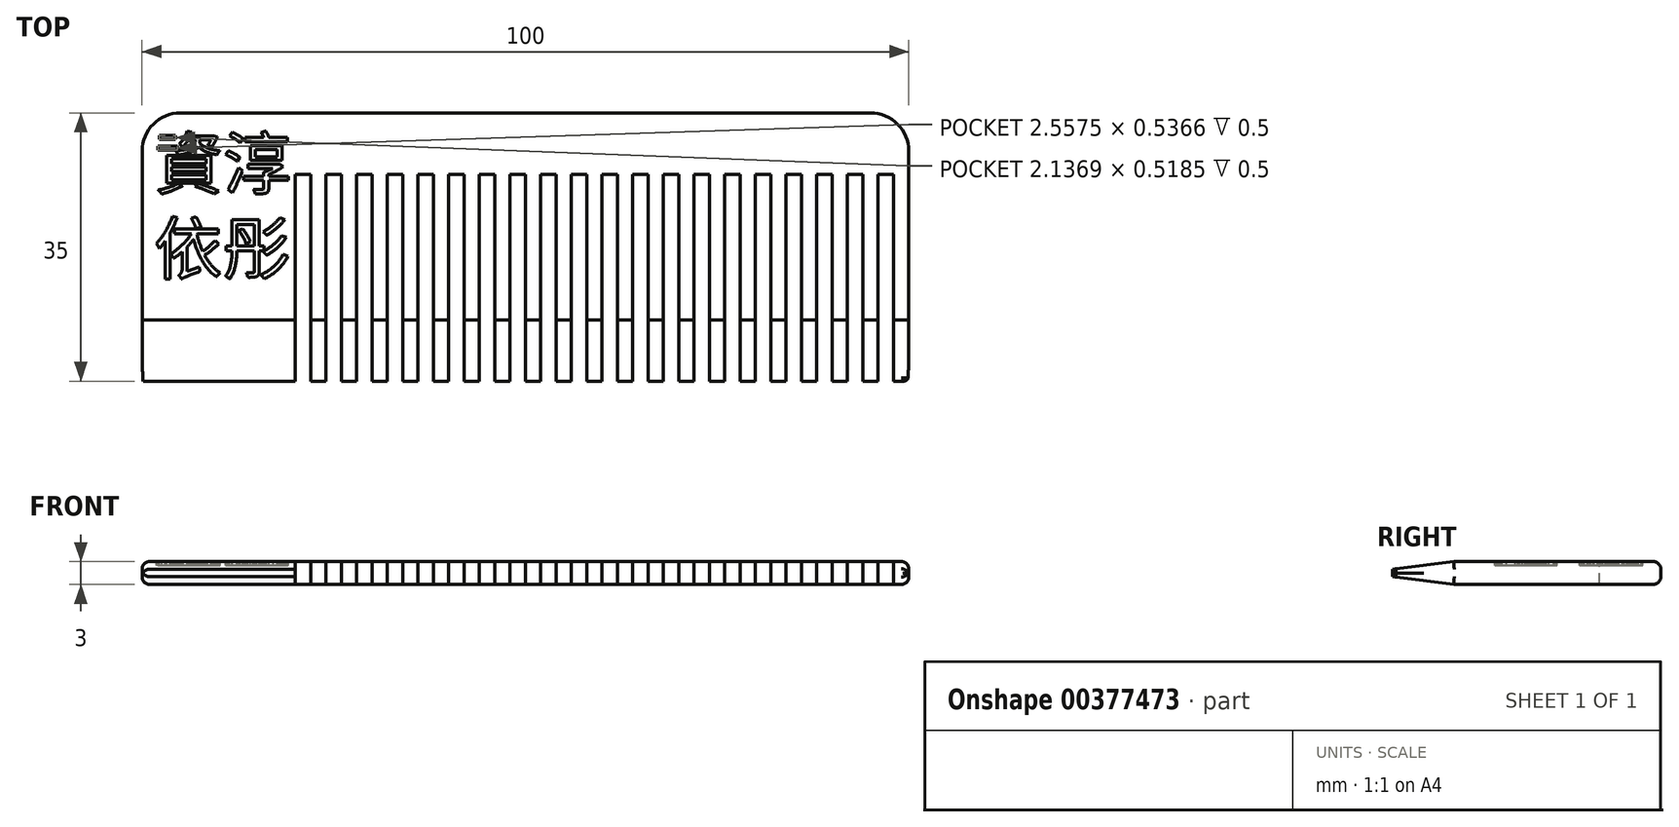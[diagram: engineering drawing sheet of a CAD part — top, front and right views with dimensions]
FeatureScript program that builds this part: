
annotation { "Feature Type Name" : "Feature", "Feature Type Description" : "" }
export const myFeature = defineFeature(function(context is Context, id is Id, definition is map)
    precondition{}
    {
        {
            var Q0;
            Q0=qCreatedBy(makeId("Top.planeOp"),FACE);
            var sketch = newSketch(context, id + "F0", { "sketchPlane" : qUnion([Q0])});
            skLineSegment(sketch, "E0.bottom", {"start": v(-53.48, 49.74) * mm, "end": v(46.52, 49.74) * mm});
            skLineSegment(sketch, "E0.top", {"start": v(-53.48, 14.74) * mm, "end": v(46.52, 14.74) * mm});
            skLineSegment(sketch, "E0.left", {"start": v(-53.48, 49.74) * mm, "end": v(-53.48, 14.74) * mm});
            skLineSegment(sketch, "E0.right", {"start": v(46.52, 49.74) * mm, "end": v(46.52, 14.74) * mm});
            skSolve(sketch);
        }
        {
            var Q0;
            Q0 = qSketchRegion(id + "F0", true);
            extrude(context, id + "F1", {"entities" : qUnion([Q0]), "depth" : 3 * mm});
        }
        {
            var Q0;
            Q0=makeQuery(id+"F1.opExtrude","CAP_FACE",FACE,{"disambiguationData":[OSD([sQuery(id+"F0.wireOp",EDGE,"E0.bottom"),sQuery(id+"F0.wireOp",EDGE,"E0.top"),sQuery(id+"F0.wireOp",EDGE,"E0.left"),sQuery(id+"F0.wireOp",EDGE,"E0.right")])],"isStart":false});
            var sketch = newSketch(context, id + "F2", { "sketchPlane" : qUnion([Q0])});
            skLineSegment(sketch, "E1.bottom", {"start": v(42.52, 41.74) * mm, "end": v(44.52, 41.74) * mm});
            skLineSegment(sketch, "E1.top", {"start": v(42.52, 6.74) * mm, "end": v(44.52, 6.74) * mm});
            skLineSegment(sketch, "E1.left", {"start": v(42.52, 41.74) * mm, "end": v(42.52, 6.74) * mm});
            skLineSegment(sketch, "E1.right", {"start": v(44.52, 41.74) * mm, "end": v(44.52, 6.74) * mm});
            skLineSegment(sketch, "E2.1.0.0", {"start": v(40.52, 41.74) * mm, "end": v(40.52, 6.74) * mm});
            skLineSegment(sketch, "E2.1.0.1", {"start": v(38.52, 41.74) * mm, "end": v(38.52, 6.74) * mm});
            skLineSegment(sketch, "E2.1.0.2", {"start": v(38.52, 6.74) * mm, "end": v(40.52, 6.74) * mm});
            skLineSegment(sketch, "E2.1.0.3", {"start": v(38.52, 41.74) * mm, "end": v(40.52, 41.74) * mm});
            skLineSegment(sketch, "E2.2.0.0", {"start": v(36.52, 41.74) * mm, "end": v(36.52, 6.74) * mm});
            skLineSegment(sketch, "E2.2.0.1", {"start": v(34.52, 41.74) * mm, "end": v(34.52, 6.74) * mm});
            skLineSegment(sketch, "E2.2.0.2", {"start": v(34.52, 6.74) * mm, "end": v(36.52, 6.74) * mm});
            skLineSegment(sketch, "E2.2.0.3", {"start": v(34.52, 41.74) * mm, "end": v(36.52, 41.74) * mm});
            skLineSegment(sketch, "E2.3.0.0", {"start": v(32.52, 41.74) * mm, "end": v(32.52, 6.74) * mm});
            skLineSegment(sketch, "E2.3.0.1", {"start": v(30.52, 41.74) * mm, "end": v(30.52, 6.74) * mm});
            skLineSegment(sketch, "E2.3.0.2", {"start": v(30.52, 6.74) * mm, "end": v(32.52, 6.74) * mm});
            skLineSegment(sketch, "E2.3.0.3", {"start": v(30.52, 41.74) * mm, "end": v(32.52, 41.74) * mm});
            skLineSegment(sketch, "E2.4.0.0", {"start": v(28.52, 41.74) * mm, "end": v(28.52, 6.74) * mm});
            skLineSegment(sketch, "E2.4.0.1", {"start": v(26.52, 41.74) * mm, "end": v(26.52, 6.74) * mm});
            skLineSegment(sketch, "E2.4.0.2", {"start": v(26.52, 6.74) * mm, "end": v(28.52, 6.74) * mm});
            skLineSegment(sketch, "E2.4.0.3", {"start": v(26.52, 41.74) * mm, "end": v(28.52, 41.74) * mm});
            skLineSegment(sketch, "E2.5.0.0", {"start": v(24.52, 41.74) * mm, "end": v(24.52, 6.74) * mm});
            skLineSegment(sketch, "E2.5.0.1", {"start": v(22.52, 41.74) * mm, "end": v(22.52, 6.74) * mm});
            skLineSegment(sketch, "E2.5.0.2", {"start": v(22.52, 6.74) * mm, "end": v(24.52, 6.74) * mm});
            skLineSegment(sketch, "E2.5.0.3", {"start": v(22.52, 41.74) * mm, "end": v(24.52, 41.74) * mm});
            skLineSegment(sketch, "E2.6.0.0", {"start": v(20.52, 41.74) * mm, "end": v(20.52, 6.74) * mm});
            skLineSegment(sketch, "E2.6.0.1", {"start": v(18.52, 41.74) * mm, "end": v(18.52, 6.74) * mm});
            skLineSegment(sketch, "E2.6.0.2", {"start": v(18.52, 6.74) * mm, "end": v(20.52, 6.74) * mm});
            skLineSegment(sketch, "E2.6.0.3", {"start": v(18.52, 41.74) * mm, "end": v(20.52, 41.74) * mm});
            skLineSegment(sketch, "E2.7.0.0", {"start": v(16.52, 41.74) * mm, "end": v(16.52, 6.74) * mm});
            skLineSegment(sketch, "E2.7.0.1", {"start": v(14.52, 41.74) * mm, "end": v(14.52, 6.74) * mm});
            skLineSegment(sketch, "E2.7.0.2", {"start": v(14.52, 6.74) * mm, "end": v(16.52, 6.74) * mm});
            skLineSegment(sketch, "E2.7.0.3", {"start": v(14.52, 41.74) * mm, "end": v(16.52, 41.74) * mm});
            skLineSegment(sketch, "E2.8.0.0", {"start": v(12.52, 41.74) * mm, "end": v(12.52, 6.74) * mm});
            skLineSegment(sketch, "E2.8.0.1", {"start": v(10.52, 41.74) * mm, "end": v(10.52, 6.74) * mm});
            skLineSegment(sketch, "E2.8.0.2", {"start": v(10.52, 6.74) * mm, "end": v(12.52, 6.74) * mm});
            skLineSegment(sketch, "E2.8.0.3", {"start": v(10.52, 41.74) * mm, "end": v(12.52, 41.74) * mm});
            skLineSegment(sketch, "E2.9.0.0", {"start": v(8.52, 41.74) * mm, "end": v(8.52, 6.74) * mm});
            skLineSegment(sketch, "E2.9.0.1", {"start": v(6.52, 41.74) * mm, "end": v(6.52, 6.74) * mm});
            skLineSegment(sketch, "E2.9.0.2", {"start": v(6.52, 6.74) * mm, "end": v(8.52, 6.74) * mm});
            skLineSegment(sketch, "E2.9.0.3", {"start": v(6.52, 41.74) * mm, "end": v(8.52, 41.74) * mm});
            skLineSegment(sketch, "E2.10.0.0", {"start": v(4.52, 41.74) * mm, "end": v(4.52, 6.74) * mm});
            skLineSegment(sketch, "E2.10.0.1", {"start": v(2.52, 41.74) * mm, "end": v(2.52, 6.74) * mm});
            skLineSegment(sketch, "E2.10.0.2", {"start": v(2.52, 6.74) * mm, "end": v(4.52, 6.74) * mm});
            skLineSegment(sketch, "E2.10.0.3", {"start": v(2.52, 41.74) * mm, "end": v(4.52, 41.74) * mm});
            skLineSegment(sketch, "E2.11.0.0", {"start": v(0.52, 41.74) * mm, "end": v(0.52, 6.74) * mm});
            skLineSegment(sketch, "E2.11.0.1", {"start": v(-1.48, 41.74) * mm, "end": v(-1.48, 6.74) * mm});
            skLineSegment(sketch, "E2.11.0.2", {"start": v(-1.48, 6.74) * mm, "end": v(0.52, 6.74) * mm});
            skLineSegment(sketch, "E2.11.0.3", {"start": v(-1.48, 41.74) * mm, "end": v(0.52, 41.74) * mm});
            skLineSegment(sketch, "E2.12.0.0", {"start": v(-3.48, 41.74) * mm, "end": v(-3.48, 6.74) * mm});
            skLineSegment(sketch, "E2.12.0.1", {"start": v(-5.48, 41.74) * mm, "end": v(-5.48, 6.74) * mm});
            skLineSegment(sketch, "E2.12.0.2", {"start": v(-5.48, 6.74) * mm, "end": v(-3.48, 6.74) * mm});
            skLineSegment(sketch, "E2.12.0.3", {"start": v(-5.48, 41.74) * mm, "end": v(-3.48, 41.74) * mm});
            skLineSegment(sketch, "E2.13.0.0", {"start": v(-7.48, 41.74) * mm, "end": v(-7.48, 6.74) * mm});
            skLineSegment(sketch, "E2.13.0.1", {"start": v(-9.48, 41.74) * mm, "end": v(-9.48, 6.74) * mm});
            skLineSegment(sketch, "E2.13.0.2", {"start": v(-9.48, 6.74) * mm, "end": v(-7.48, 6.74) * mm});
            skLineSegment(sketch, "E2.13.0.3", {"start": v(-9.48, 41.74) * mm, "end": v(-7.48, 41.74) * mm});
            skLineSegment(sketch, "E2.14.0.0", {"start": v(-11.48, 41.74) * mm, "end": v(-11.48, 6.74) * mm});
            skLineSegment(sketch, "E2.14.0.1", {"start": v(-13.48, 41.74) * mm, "end": v(-13.48, 6.74) * mm});
            skLineSegment(sketch, "E2.14.0.2", {"start": v(-13.48, 6.74) * mm, "end": v(-11.48, 6.74) * mm});
            skLineSegment(sketch, "E2.14.0.3", {"start": v(-13.48, 41.74) * mm, "end": v(-11.48, 41.74) * mm});
            skLineSegment(sketch, "E2.15.0.0", {"start": v(-15.48, 41.74) * mm, "end": v(-15.48, 6.74) * mm});
            skLineSegment(sketch, "E2.15.0.1", {"start": v(-17.48, 41.74) * mm, "end": v(-17.48, 6.74) * mm});
            skLineSegment(sketch, "E2.15.0.2", {"start": v(-17.48, 6.74) * mm, "end": v(-15.48, 6.74) * mm});
            skLineSegment(sketch, "E2.15.0.3", {"start": v(-17.48, 41.74) * mm, "end": v(-15.48, 41.74) * mm});
            skLineSegment(sketch, "E2.16.0.0", {"start": v(-19.48, 41.74) * mm, "end": v(-19.48, 6.74) * mm});
            skLineSegment(sketch, "E2.16.0.1", {"start": v(-21.48, 41.74) * mm, "end": v(-21.48, 6.74) * mm});
            skLineSegment(sketch, "E2.16.0.2", {"start": v(-21.48, 6.74) * mm, "end": v(-19.48, 6.74) * mm});
            skLineSegment(sketch, "E2.16.0.3", {"start": v(-21.48, 41.74) * mm, "end": v(-19.48, 41.74) * mm});
            skLineSegment(sketch, "E2.17.0.0", {"start": v(-23.48, 41.74) * mm, "end": v(-23.48, 6.74) * mm});
            skLineSegment(sketch, "E2.17.0.1", {"start": v(-25.48, 41.74) * mm, "end": v(-25.48, 6.74) * mm});
            skLineSegment(sketch, "E2.17.0.2", {"start": v(-25.48, 6.74) * mm, "end": v(-23.48, 6.74) * mm});
            skLineSegment(sketch, "E2.17.0.3", {"start": v(-25.48, 41.74) * mm, "end": v(-23.48, 41.74) * mm});
            skLineSegment(sketch, "E2.18.0.0", {"start": v(-27.48, 41.74) * mm, "end": v(-27.48, 6.74) * mm});
            skLineSegment(sketch, "E2.18.0.1", {"start": v(-29.48, 41.74) * mm, "end": v(-29.48, 6.74) * mm});
            skLineSegment(sketch, "E2.18.0.2", {"start": v(-29.48, 6.74) * mm, "end": v(-27.48, 6.74) * mm});
            skLineSegment(sketch, "E2.18.0.3", {"start": v(-29.48, 41.74) * mm, "end": v(-27.48, 41.74) * mm});
            skLineSegment(sketch, "E2.19.0.0", {"start": v(-31.48, 41.74) * mm, "end": v(-31.48, 6.74) * mm});
            skLineSegment(sketch, "E2.19.0.1", {"start": v(-33.48, 41.74) * mm, "end": v(-33.48, 6.74) * mm});
            skLineSegment(sketch, "E2.19.0.2", {"start": v(-33.48, 6.74) * mm, "end": v(-31.48, 6.74) * mm});
            skLineSegment(sketch, "E2.19.0.3", {"start": v(-33.48, 41.74) * mm, "end": v(-31.48, 41.74) * mm});
            skLineSegment(sketch, "E2.direction1", {"start": v(42.52, 6.74) * mm, "end": v(38.52, 6.74) * mm, "construction": true});
            skSolve(sketch);
        }
        {
            var Q0;
            Q0=makeQuery(id+"F1.opExtrude","CAP_EDGE",EDGE,{"disambiguationData":[OSD([sQuery(id+"F0.wireOp",EDGE,"E0.top")])],"isStart":true});
            var Q1;
            Q1=makeQuery(id+"F1.opExtrude","CAP_EDGE",EDGE,{"disambiguationData":[OSD([sQuery(id+"F0.wireOp",EDGE,"E0.top")])],"isStart":false});
            chamfer(context, id + "F3", {"entities" : qUnion([Q0, Q1]), "chamferType" : ChamferType.TWO_OFFSETS, "width1" : 1 * mm, "oppositeDirection" : false, "width2" : 8 * mm, "tangentPropagation" : true});
        }
        {
            var Q0;
            Q0 = qSketchRegion(id + "F2", true);
            extrude(context, id + "F4", {"entities" : qUnion([Q0]), "operationType" : NewBodyOperationType.REMOVE, "oppositeDirection" : true, "depth" : 25 * mm});
        }
        {
            var Q0;
            Q0=makeQuery(id+"F1.opExtrude","CAP_EDGE",EDGE,{"disambiguationData":[OSD([sQuery(id+"F0.wireOp",EDGE,"E0.left")])],"isStart":false});
            var Q1;
            Q1=makeQuery(id+"F1.opExtrude","CAP_EDGE",EDGE,{"disambiguationData":[OSD([sQuery(id+"F0.wireOp",EDGE,"E0.left")])],"isStart":true});
            var Q2;
            Q2=makeQuery(id+"F1.opExtrude","CAP_EDGE",EDGE,{"disambiguationData":[OSD([sQuery(id+"F0.wireOp",EDGE,"E0.bottom")])],"isStart":false});
            var Q3;
            Q3=makeQuery(id+"F1.opExtrude","CAP_EDGE",EDGE,{"disambiguationData":[OSD([sQuery(id+"F0.wireOp",EDGE,"E0.bottom")])],"isStart":true});
            var Q4;
            Q4=makeQuery(id+"F1.opExtrude","CAP_EDGE",EDGE,{"disambiguationData":[OSD([sQuery(id+"F0.wireOp",EDGE,"E0.right")])],"isStart":false});
            var Q5;
            Q5=makeQuery(id+"F1.opExtrude","CAP_EDGE",EDGE,{"disambiguationData":[OSD([sQuery(id+"F0.wireOp",EDGE,"E0.right")])],"isStart":true});
            var Q6;
            Q6=makeQuery(id+"F3.opChamfer","BLEND_EDGE",EDGE,{"blendedFrom":[makeQuery(id+"F1.opExtrude","CAP_EDGE",EDGE,{"disambiguationData":[OSD([sQuery(id+"F0.wireOp",EDGE,"E0.top")])],"isStart":false}),makeQuery(id+"F1.opExtrude","SWEPT_FACE",FACE,{"disambiguationData":[OSD([sQuery(id+"F0.wireOp",EDGE,"E0.left")])]})],"blendedInto":[makeQuery(id+"F1.opExtrude","SWEPT_FACE",FACE,{"disambiguationData":[OSD([sQuery(id+"F0.wireOp",EDGE,"E0.left")])]})]});
            var Q7;
            Q7=makeQuery(id+"F3.opChamfer","BLEND_EDGE",EDGE,{"blendedFrom":[makeQuery(id+"F1.opExtrude","CAP_EDGE",EDGE,{"disambiguationData":[OSD([sQuery(id+"F0.wireOp",EDGE,"E0.top")])],"isStart":true}),makeQuery(id+"F1.opExtrude","SWEPT_FACE",FACE,{"disambiguationData":[OSD([sQuery(id+"F0.wireOp",EDGE,"E0.left")])]})],"blendedInto":[makeQuery(id+"F1.opExtrude","SWEPT_FACE",FACE,{"disambiguationData":[OSD([sQuery(id+"F0.wireOp",EDGE,"E0.left")])]})]});
            var Q8;
            Q8=makeQuery(id+"F3.opChamfer","BLEND_EDGE",EDGE,{"blendedFrom":[makeQuery(id+"F1.opExtrude","CAP_EDGE",EDGE,{"disambiguationData":[OSD([sQuery(id+"F0.wireOp",EDGE,"E0.top")])],"isStart":true}),makeQuery(id+"F1.opExtrude","SWEPT_FACE",FACE,{"disambiguationData":[OSD([sQuery(id+"F0.wireOp",EDGE,"E0.right")])]})],"blendedInto":[makeQuery(id+"F1.opExtrude","SWEPT_FACE",FACE,{"disambiguationData":[OSD([sQuery(id+"F0.wireOp",EDGE,"E0.right")])]})]});
            var Q9;
            Q9=makeQuery(id+"F3.opChamfer","BLEND_EDGE",EDGE,{"blendedFrom":[makeQuery(id+"F1.opExtrude","CAP_EDGE",EDGE,{"disambiguationData":[OSD([sQuery(id+"F0.wireOp",EDGE,"E0.top")])],"isStart":false}),makeQuery(id+"F1.opExtrude","SWEPT_FACE",FACE,{"disambiguationData":[OSD([sQuery(id+"F0.wireOp",EDGE,"E0.right")])]})],"blendedInto":[makeQuery(id+"F1.opExtrude","SWEPT_FACE",FACE,{"disambiguationData":[OSD([sQuery(id+"F0.wireOp",EDGE,"E0.right")])]})]});
            fillet(context, id + "F5", {"entities" : qUnion([Q0, Q1, Q2, Q3, Q4, Q5, Q6, Q7, Q8, Q9]), "radius" : 1 * mm, "tangentPropagation" : true, "allowEdgeOverflow" : false});
        }
        {
            var Q0;
            Q0=makeQuery(id+"F1.opExtrude","SWEPT_EDGE",EDGE,{"disambiguationData":[OSD([sQuery(id+"F0.wireOp",EDGE,"E0.bottom"),sQuery(id+"F0.wireOp",EDGE,"E0.left")])]});
            var Q1;
            Q1=makeQuery(id+"F5.opFillet","BLEND_EDGE",EDGE,{"blendedFrom":[makeQuery(id+"F1.opExtrude","CAP_EDGE",EDGE,{"disambiguationData":[OSD([sQuery(id+"F0.wireOp",EDGE,"E0.bottom")])],"isStart":false}),makeQuery(id+"F1.opExtrude","CAP_EDGE",EDGE,{"disambiguationData":[OSD([sQuery(id+"F0.wireOp",EDGE,"E0.right")])],"isStart":false})],"blendedInto":[]});
            fillet(context, id + "F6", {"entities" : qUnion([Q0, Q1]), "radius" : 5 * mm, "tangentPropagation" : true, "allowEdgeOverflow" : false});
        }
        {
            var Q0;
            {var subQ0=sQuery(id+"F0.wireOp",EDGE,"E0.top");var subQ1=makeQuery(id+"F1.opExtrude","SWEPT_FACE",FACE,{"disambiguationData":[OSD([subQ0])]});var subQ2=makeQuery(id+"F1.opExtrude","CAP_EDGE",EDGE,{"disambiguationData":[OSD([subQ0])],"isStart":false});Q0=makeQuery(id+"F4.boolean.opBoolean","SPLIT",EDGE,{"disambiguationData":[TD([makeQuery(id+"F4.opExtrude","SWEPT_FACE",FACE,{"disambiguationData":[OSD([sQuery(id+"F2.wireOp",EDGE,"E2.18.0.1")])]})])],"derivedFrom":makeQuery(id+"F3.opChamfer","BLEND_EDGE",EDGE,{"blendedFrom":[subQ2,subQ1],"blendedInto":[subQ1]})});}
            var Q1;
            {var subQ0=sQuery(id+"F0.wireOp",EDGE,"E0.top");var subQ1=makeQuery(id+"F1.opExtrude","SWEPT_FACE",FACE,{"disambiguationData":[OSD([subQ0])]});var subQ2=makeQuery(id+"F1.opExtrude","CAP_EDGE",EDGE,{"disambiguationData":[OSD([subQ0])],"isStart":false});Q1=makeQuery(id+"F4.boolean.opBoolean","SPLIT",EDGE,{"disambiguationData":[TD([makeQuery(id+"F4.opExtrude","SWEPT_FACE",FACE,{"disambiguationData":[OSD([sQuery(id+"F2.wireOp",EDGE,"E2.17.0.1")])]})])],"derivedFrom":makeQuery(id+"F3.opChamfer","BLEND_EDGE",EDGE,{"blendedFrom":[subQ2,subQ1],"blendedInto":[subQ1]})});}
            var Q2;
            {var subQ0=sQuery(id+"F0.wireOp",EDGE,"E0.top");var subQ1=makeQuery(id+"F1.opExtrude","SWEPT_FACE",FACE,{"disambiguationData":[OSD([subQ0])]});var subQ2=makeQuery(id+"F1.opExtrude","CAP_EDGE",EDGE,{"disambiguationData":[OSD([subQ0])],"isStart":false});Q2=makeQuery(id+"F4.boolean.opBoolean","SPLIT",EDGE,{"disambiguationData":[TD([makeQuery(id+"F4.opExtrude","SWEPT_FACE",FACE,{"disambiguationData":[OSD([sQuery(id+"F2.wireOp",EDGE,"E2.16.0.1")])]})])],"derivedFrom":makeQuery(id+"F3.opChamfer","BLEND_EDGE",EDGE,{"blendedFrom":[subQ2,subQ1],"blendedInto":[subQ1]})});}
            var Q3;
            {var subQ0=sQuery(id+"F0.wireOp",EDGE,"E0.top");var subQ1=makeQuery(id+"F1.opExtrude","SWEPT_FACE",FACE,{"disambiguationData":[OSD([subQ0])]});var subQ2=makeQuery(id+"F1.opExtrude","CAP_EDGE",EDGE,{"disambiguationData":[OSD([subQ0])],"isStart":false});Q3=makeQuery(id+"F4.boolean.opBoolean","SPLIT",EDGE,{"disambiguationData":[TD([makeQuery(id+"F4.opExtrude","SWEPT_FACE",FACE,{"disambiguationData":[OSD([sQuery(id+"F2.wireOp",EDGE,"E2.15.0.1")])]})])],"derivedFrom":makeQuery(id+"F3.opChamfer","BLEND_EDGE",EDGE,{"blendedFrom":[subQ2,subQ1],"blendedInto":[subQ1]})});}
            var Q4;
            {var subQ0=sQuery(id+"F0.wireOp",EDGE,"E0.top");var subQ1=makeQuery(id+"F1.opExtrude","SWEPT_FACE",FACE,{"disambiguationData":[OSD([subQ0])]});var subQ2=makeQuery(id+"F1.opExtrude","CAP_EDGE",EDGE,{"disambiguationData":[OSD([subQ0])],"isStart":false});Q4=makeQuery(id+"F4.boolean.opBoolean","SPLIT",EDGE,{"disambiguationData":[TD([makeQuery(id+"F4.opExtrude","SWEPT_FACE",FACE,{"disambiguationData":[OSD([sQuery(id+"F2.wireOp",EDGE,"E2.14.0.1")])]})])],"derivedFrom":makeQuery(id+"F3.opChamfer","BLEND_EDGE",EDGE,{"blendedFrom":[subQ2,subQ1],"blendedInto":[subQ1]})});}
            var Q5;
            {var subQ0=sQuery(id+"F0.wireOp",EDGE,"E0.top");var subQ1=makeQuery(id+"F1.opExtrude","SWEPT_FACE",FACE,{"disambiguationData":[OSD([subQ0])]});var subQ2=makeQuery(id+"F1.opExtrude","CAP_EDGE",EDGE,{"disambiguationData":[OSD([subQ0])],"isStart":false});Q5=makeQuery(id+"F4.boolean.opBoolean","SPLIT",EDGE,{"disambiguationData":[TD([makeQuery(id+"F4.opExtrude","SWEPT_FACE",FACE,{"disambiguationData":[OSD([sQuery(id+"F2.wireOp",EDGE,"E2.13.0.1")])]})])],"derivedFrom":makeQuery(id+"F3.opChamfer","BLEND_EDGE",EDGE,{"blendedFrom":[subQ2,subQ1],"blendedInto":[subQ1]})});}
            var Q6;
            {var subQ0=sQuery(id+"F0.wireOp",EDGE,"E0.top");var subQ1=makeQuery(id+"F1.opExtrude","SWEPT_FACE",FACE,{"disambiguationData":[OSD([subQ0])]});var subQ2=makeQuery(id+"F1.opExtrude","CAP_EDGE",EDGE,{"disambiguationData":[OSD([subQ0])],"isStart":false});Q6=makeQuery(id+"F4.boolean.opBoolean","SPLIT",EDGE,{"disambiguationData":[TD([makeQuery(id+"F4.opExtrude","SWEPT_FACE",FACE,{"disambiguationData":[OSD([sQuery(id+"F2.wireOp",EDGE,"E2.12.0.1")])]})])],"derivedFrom":makeQuery(id+"F3.opChamfer","BLEND_EDGE",EDGE,{"blendedFrom":[subQ2,subQ1],"blendedInto":[subQ1]})});}
            var Q7;
            {var subQ0=sQuery(id+"F0.wireOp",EDGE,"E0.top");var subQ1=makeQuery(id+"F1.opExtrude","SWEPT_FACE",FACE,{"disambiguationData":[OSD([subQ0])]});var subQ2=makeQuery(id+"F1.opExtrude","CAP_EDGE",EDGE,{"disambiguationData":[OSD([subQ0])],"isStart":false});Q7=makeQuery(id+"F4.boolean.opBoolean","SPLIT",EDGE,{"disambiguationData":[TD([makeQuery(id+"F4.opExtrude","SWEPT_FACE",FACE,{"disambiguationData":[OSD([sQuery(id+"F2.wireOp",EDGE,"E2.11.0.1")])]})])],"derivedFrom":makeQuery(id+"F3.opChamfer","BLEND_EDGE",EDGE,{"blendedFrom":[subQ2,subQ1],"blendedInto":[subQ1]})});}
            var Q8;
            {var subQ0=sQuery(id+"F0.wireOp",EDGE,"E0.top");var subQ1=makeQuery(id+"F1.opExtrude","SWEPT_FACE",FACE,{"disambiguationData":[OSD([subQ0])]});var subQ2=makeQuery(id+"F1.opExtrude","CAP_EDGE",EDGE,{"disambiguationData":[OSD([subQ0])],"isStart":false});Q8=makeQuery(id+"F4.boolean.opBoolean","SPLIT",EDGE,{"disambiguationData":[TD([makeQuery(id+"F4.opExtrude","SWEPT_FACE",FACE,{"disambiguationData":[OSD([sQuery(id+"F2.wireOp",EDGE,"E2.10.0.1")])]})])],"derivedFrom":makeQuery(id+"F3.opChamfer","BLEND_EDGE",EDGE,{"blendedFrom":[subQ2,subQ1],"blendedInto":[subQ1]})});}
            var Q9;
            {var subQ0=sQuery(id+"F0.wireOp",EDGE,"E0.top");var subQ1=makeQuery(id+"F1.opExtrude","SWEPT_FACE",FACE,{"disambiguationData":[OSD([subQ0])]});var subQ2=makeQuery(id+"F1.opExtrude","CAP_EDGE",EDGE,{"disambiguationData":[OSD([subQ0])],"isStart":false});Q9=makeQuery(id+"F4.boolean.opBoolean","SPLIT",EDGE,{"disambiguationData":[TD([makeQuery(id+"F4.opExtrude","SWEPT_FACE",FACE,{"disambiguationData":[OSD([sQuery(id+"F2.wireOp",EDGE,"E2.9.0.1")])]})])],"derivedFrom":makeQuery(id+"F3.opChamfer","BLEND_EDGE",EDGE,{"blendedFrom":[subQ2,subQ1],"blendedInto":[subQ1]})});}
            var Q10;
            {var subQ0=sQuery(id+"F0.wireOp",EDGE,"E0.top");var subQ1=makeQuery(id+"F1.opExtrude","SWEPT_FACE",FACE,{"disambiguationData":[OSD([subQ0])]});var subQ2=makeQuery(id+"F1.opExtrude","CAP_EDGE",EDGE,{"disambiguationData":[OSD([subQ0])],"isStart":false});Q10=makeQuery(id+"F4.boolean.opBoolean","SPLIT",EDGE,{"disambiguationData":[TD([makeQuery(id+"F4.opExtrude","SWEPT_FACE",FACE,{"disambiguationData":[OSD([sQuery(id+"F2.wireOp",EDGE,"E2.8.0.1")])]})])],"derivedFrom":makeQuery(id+"F3.opChamfer","BLEND_EDGE",EDGE,{"blendedFrom":[subQ2,subQ1],"blendedInto":[subQ1]})});}
            var Q11;
            {var subQ0=sQuery(id+"F0.wireOp",EDGE,"E0.top");var subQ1=makeQuery(id+"F1.opExtrude","SWEPT_FACE",FACE,{"disambiguationData":[OSD([subQ0])]});var subQ2=makeQuery(id+"F1.opExtrude","CAP_EDGE",EDGE,{"disambiguationData":[OSD([subQ0])],"isStart":false});Q11=makeQuery(id+"F4.boolean.opBoolean","SPLIT",EDGE,{"disambiguationData":[TD([makeQuery(id+"F4.opExtrude","SWEPT_FACE",FACE,{"disambiguationData":[OSD([sQuery(id+"F2.wireOp",EDGE,"E2.7.0.1")])]})])],"derivedFrom":makeQuery(id+"F3.opChamfer","BLEND_EDGE",EDGE,{"blendedFrom":[subQ2,subQ1],"blendedInto":[subQ1]})});}
            var Q12;
            {var subQ0=sQuery(id+"F0.wireOp",EDGE,"E0.top");var subQ1=makeQuery(id+"F1.opExtrude","SWEPT_FACE",FACE,{"disambiguationData":[OSD([subQ0])]});var subQ2=makeQuery(id+"F1.opExtrude","CAP_EDGE",EDGE,{"disambiguationData":[OSD([subQ0])],"isStart":false});Q12=makeQuery(id+"F4.boolean.opBoolean","SPLIT",EDGE,{"disambiguationData":[TD([makeQuery(id+"F4.opExtrude","SWEPT_FACE",FACE,{"disambiguationData":[OSD([sQuery(id+"F2.wireOp",EDGE,"E2.5.0.1")])]})])],"derivedFrom":makeQuery(id+"F3.opChamfer","BLEND_EDGE",EDGE,{"blendedFrom":[subQ2,subQ1],"blendedInto":[subQ1]})});}
            var Q13;
            {var subQ0=sQuery(id+"F0.wireOp",EDGE,"E0.top");var subQ1=makeQuery(id+"F1.opExtrude","SWEPT_FACE",FACE,{"disambiguationData":[OSD([subQ0])]});var subQ2=makeQuery(id+"F1.opExtrude","CAP_EDGE",EDGE,{"disambiguationData":[OSD([subQ0])],"isStart":false});Q13=makeQuery(id+"F4.boolean.opBoolean","SPLIT",EDGE,{"disambiguationData":[TD([makeQuery(id+"F4.opExtrude","SWEPT_FACE",FACE,{"disambiguationData":[OSD([sQuery(id+"F2.wireOp",EDGE,"E2.4.0.1")])]})])],"derivedFrom":makeQuery(id+"F3.opChamfer","BLEND_EDGE",EDGE,{"blendedFrom":[subQ2,subQ1],"blendedInto":[subQ1]})});}
            var Q14;
            {var subQ0=sQuery(id+"F0.wireOp",EDGE,"E0.top");var subQ1=makeQuery(id+"F1.opExtrude","SWEPT_FACE",FACE,{"disambiguationData":[OSD([subQ0])]});var subQ2=makeQuery(id+"F1.opExtrude","CAP_EDGE",EDGE,{"disambiguationData":[OSD([subQ0])],"isStart":false});Q14=makeQuery(id+"F4.boolean.opBoolean","SPLIT",EDGE,{"disambiguationData":[TD([makeQuery(id+"F4.opExtrude","SWEPT_FACE",FACE,{"disambiguationData":[OSD([sQuery(id+"F2.wireOp",EDGE,"E2.3.0.1")])]})])],"derivedFrom":makeQuery(id+"F3.opChamfer","BLEND_EDGE",EDGE,{"blendedFrom":[subQ2,subQ1],"blendedInto":[subQ1]})});}
            var Q15;
            {var subQ0=sQuery(id+"F0.wireOp",EDGE,"E0.top");var subQ1=makeQuery(id+"F1.opExtrude","SWEPT_FACE",FACE,{"disambiguationData":[OSD([subQ0])]});var subQ2=makeQuery(id+"F1.opExtrude","CAP_EDGE",EDGE,{"disambiguationData":[OSD([subQ0])],"isStart":false});Q15=makeQuery(id+"F4.boolean.opBoolean","SPLIT",EDGE,{"disambiguationData":[TD([makeQuery(id+"F4.opExtrude","SWEPT_FACE",FACE,{"disambiguationData":[OSD([sQuery(id+"F2.wireOp",EDGE,"E2.2.0.1")])]})])],"derivedFrom":makeQuery(id+"F3.opChamfer","BLEND_EDGE",EDGE,{"blendedFrom":[subQ2,subQ1],"blendedInto":[subQ1]})});}
            var Q16;
            {var subQ0=sQuery(id+"F0.wireOp",EDGE,"E0.top");var subQ1=makeQuery(id+"F1.opExtrude","SWEPT_FACE",FACE,{"disambiguationData":[OSD([subQ0])]});var subQ2=makeQuery(id+"F1.opExtrude","CAP_EDGE",EDGE,{"disambiguationData":[OSD([subQ0])],"isStart":false});Q16=makeQuery(id+"F4.boolean.opBoolean","SPLIT",EDGE,{"disambiguationData":[TD([makeQuery(id+"F4.opExtrude","SWEPT_FACE",FACE,{"disambiguationData":[OSD([sQuery(id+"F2.wireOp",EDGE,"E2.1.0.1")])]})])],"derivedFrom":makeQuery(id+"F3.opChamfer","BLEND_EDGE",EDGE,{"blendedFrom":[subQ2,subQ1],"blendedInto":[subQ1]})});}
            var Q17;
            {var subQ0=sQuery(id+"F0.wireOp",EDGE,"E0.top");var subQ1=makeQuery(id+"F1.opExtrude","SWEPT_FACE",FACE,{"disambiguationData":[OSD([subQ0])]});var subQ2=makeQuery(id+"F1.opExtrude","CAP_EDGE",EDGE,{"disambiguationData":[OSD([subQ0])],"isStart":false});Q17=makeQuery(id+"F4.boolean.opBoolean","SPLIT",EDGE,{"disambiguationData":[TD([makeQuery(id+"F4.opExtrude","SWEPT_FACE",FACE,{"disambiguationData":[OSD([sQuery(id+"F2.wireOp",EDGE,"E1.left")])]})])],"derivedFrom":makeQuery(id+"F3.opChamfer","BLEND_EDGE",EDGE,{"blendedFrom":[subQ2,subQ1],"blendedInto":[subQ1]})});}
            var Q18;
            {var subQ0=sQuery(id+"F0.wireOp",EDGE,"E0.top");var subQ1=makeQuery(id+"F1.opExtrude","SWEPT_FACE",FACE,{"disambiguationData":[OSD([subQ0])]});var subQ2=makeQuery(id+"F1.opExtrude","CAP_EDGE",EDGE,{"disambiguationData":[OSD([subQ0])],"isStart":false});Q18=makeQuery(id+"F4.boolean.opBoolean","SPLIT",EDGE,{"disambiguationData":[TD([makeQuery(id+"F4.opExtrude","SWEPT_FACE",FACE,{"disambiguationData":[OSD([sQuery(id+"F2.wireOp",EDGE,"E2.6.0.1")])]})])],"derivedFrom":makeQuery(id+"F3.opChamfer","BLEND_EDGE",EDGE,{"blendedFrom":[subQ2,subQ1],"blendedInto":[subQ1]})});}
            var Q19;
            {var subQ0=sQuery(id+"F0.wireOp",EDGE,"E0.top");var subQ1=makeQuery(id+"F1.opExtrude","SWEPT_FACE",FACE,{"disambiguationData":[OSD([subQ0])]});var subQ2=makeQuery(id+"F1.opExtrude","CAP_EDGE",EDGE,{"disambiguationData":[OSD([subQ0])],"isStart":true});Q19=makeQuery(id+"F4.boolean.opBoolean","SPLIT",EDGE,{"disambiguationData":[TD([makeQuery(id+"F4.opExtrude","SWEPT_FACE",FACE,{"disambiguationData":[OSD([sQuery(id+"F2.wireOp",EDGE,"E2.18.0.1")])]})])],"derivedFrom":makeQuery(id+"F3.opChamfer","BLEND_EDGE",EDGE,{"blendedFrom":[subQ2,subQ1],"blendedInto":[subQ1]})});}
            var Q20;
            {var subQ0=sQuery(id+"F0.wireOp",EDGE,"E0.top");var subQ1=makeQuery(id+"F1.opExtrude","SWEPT_FACE",FACE,{"disambiguationData":[OSD([subQ0])]});var subQ2=makeQuery(id+"F1.opExtrude","CAP_EDGE",EDGE,{"disambiguationData":[OSD([subQ0])],"isStart":true});Q20=makeQuery(id+"F4.boolean.opBoolean","SPLIT",EDGE,{"disambiguationData":[TD([makeQuery(id+"F4.opExtrude","SWEPT_FACE",FACE,{"disambiguationData":[OSD([sQuery(id+"F2.wireOp",EDGE,"E2.17.0.1")])]})])],"derivedFrom":makeQuery(id+"F3.opChamfer","BLEND_EDGE",EDGE,{"blendedFrom":[subQ2,subQ1],"blendedInto":[subQ1]})});}
            var Q21;
            {var subQ0=sQuery(id+"F0.wireOp",EDGE,"E0.top");var subQ1=makeQuery(id+"F1.opExtrude","SWEPT_FACE",FACE,{"disambiguationData":[OSD([subQ0])]});var subQ2=makeQuery(id+"F1.opExtrude","CAP_EDGE",EDGE,{"disambiguationData":[OSD([subQ0])],"isStart":true});Q21=makeQuery(id+"F4.boolean.opBoolean","SPLIT",EDGE,{"disambiguationData":[TD([makeQuery(id+"F4.opExtrude","SWEPT_FACE",FACE,{"disambiguationData":[OSD([sQuery(id+"F2.wireOp",EDGE,"E2.16.0.1")])]})])],"derivedFrom":makeQuery(id+"F3.opChamfer","BLEND_EDGE",EDGE,{"blendedFrom":[subQ2,subQ1],"blendedInto":[subQ1]})});}
            var Q22;
            {var subQ0=sQuery(id+"F0.wireOp",EDGE,"E0.top");var subQ1=makeQuery(id+"F1.opExtrude","SWEPT_FACE",FACE,{"disambiguationData":[OSD([subQ0])]});var subQ2=makeQuery(id+"F1.opExtrude","CAP_EDGE",EDGE,{"disambiguationData":[OSD([subQ0])],"isStart":true});Q22=makeQuery(id+"F4.boolean.opBoolean","SPLIT",EDGE,{"disambiguationData":[TD([makeQuery(id+"F4.opExtrude","SWEPT_FACE",FACE,{"disambiguationData":[OSD([sQuery(id+"F2.wireOp",EDGE,"E2.15.0.1")])]})])],"derivedFrom":makeQuery(id+"F3.opChamfer","BLEND_EDGE",EDGE,{"blendedFrom":[subQ2,subQ1],"blendedInto":[subQ1]})});}
            var Q23;
            {var subQ0=sQuery(id+"F0.wireOp",EDGE,"E0.top");var subQ1=makeQuery(id+"F1.opExtrude","SWEPT_FACE",FACE,{"disambiguationData":[OSD([subQ0])]});var subQ2=makeQuery(id+"F1.opExtrude","CAP_EDGE",EDGE,{"disambiguationData":[OSD([subQ0])],"isStart":true});Q23=makeQuery(id+"F4.boolean.opBoolean","SPLIT",EDGE,{"disambiguationData":[TD([makeQuery(id+"F4.opExtrude","SWEPT_FACE",FACE,{"disambiguationData":[OSD([sQuery(id+"F2.wireOp",EDGE,"E2.14.0.1")])]})])],"derivedFrom":makeQuery(id+"F3.opChamfer","BLEND_EDGE",EDGE,{"blendedFrom":[subQ2,subQ1],"blendedInto":[subQ1]})});}
            var Q24;
            {var subQ0=sQuery(id+"F0.wireOp",EDGE,"E0.top");var subQ1=makeQuery(id+"F1.opExtrude","SWEPT_FACE",FACE,{"disambiguationData":[OSD([subQ0])]});var subQ2=makeQuery(id+"F1.opExtrude","CAP_EDGE",EDGE,{"disambiguationData":[OSD([subQ0])],"isStart":true});Q24=makeQuery(id+"F4.boolean.opBoolean","SPLIT",EDGE,{"disambiguationData":[TD([makeQuery(id+"F4.opExtrude","SWEPT_FACE",FACE,{"disambiguationData":[OSD([sQuery(id+"F2.wireOp",EDGE,"E2.13.0.1")])]})])],"derivedFrom":makeQuery(id+"F3.opChamfer","BLEND_EDGE",EDGE,{"blendedFrom":[subQ2,subQ1],"blendedInto":[subQ1]})});}
            var Q25;
            {var subQ0=sQuery(id+"F0.wireOp",EDGE,"E0.top");var subQ1=makeQuery(id+"F1.opExtrude","SWEPT_FACE",FACE,{"disambiguationData":[OSD([subQ0])]});var subQ2=makeQuery(id+"F1.opExtrude","CAP_EDGE",EDGE,{"disambiguationData":[OSD([subQ0])],"isStart":true});Q25=makeQuery(id+"F4.boolean.opBoolean","SPLIT",EDGE,{"disambiguationData":[TD([makeQuery(id+"F4.opExtrude","SWEPT_FACE",FACE,{"disambiguationData":[OSD([sQuery(id+"F2.wireOp",EDGE,"E2.12.0.1")])]})])],"derivedFrom":makeQuery(id+"F3.opChamfer","BLEND_EDGE",EDGE,{"blendedFrom":[subQ2,subQ1],"blendedInto":[subQ1]})});}
            var Q26;
            {var subQ0=sQuery(id+"F0.wireOp",EDGE,"E0.top");var subQ1=makeQuery(id+"F1.opExtrude","SWEPT_FACE",FACE,{"disambiguationData":[OSD([subQ0])]});var subQ2=makeQuery(id+"F1.opExtrude","CAP_EDGE",EDGE,{"disambiguationData":[OSD([subQ0])],"isStart":true});Q26=makeQuery(id+"F4.boolean.opBoolean","SPLIT",EDGE,{"disambiguationData":[TD([makeQuery(id+"F4.opExtrude","SWEPT_FACE",FACE,{"disambiguationData":[OSD([sQuery(id+"F2.wireOp",EDGE,"E2.11.0.1")])]})])],"derivedFrom":makeQuery(id+"F3.opChamfer","BLEND_EDGE",EDGE,{"blendedFrom":[subQ2,subQ1],"blendedInto":[subQ1]})});}
            var Q27;
            {var subQ0=sQuery(id+"F0.wireOp",EDGE,"E0.top");var subQ1=makeQuery(id+"F1.opExtrude","SWEPT_FACE",FACE,{"disambiguationData":[OSD([subQ0])]});var subQ2=makeQuery(id+"F1.opExtrude","CAP_EDGE",EDGE,{"disambiguationData":[OSD([subQ0])],"isStart":true});Q27=makeQuery(id+"F4.boolean.opBoolean","SPLIT",EDGE,{"disambiguationData":[TD([makeQuery(id+"F4.opExtrude","SWEPT_FACE",FACE,{"disambiguationData":[OSD([sQuery(id+"F2.wireOp",EDGE,"E2.10.0.1")])]})])],"derivedFrom":makeQuery(id+"F3.opChamfer","BLEND_EDGE",EDGE,{"blendedFrom":[subQ2,subQ1],"blendedInto":[subQ1]})});}
            var Q28;
            {var subQ0=sQuery(id+"F0.wireOp",EDGE,"E0.top");var subQ1=makeQuery(id+"F1.opExtrude","SWEPT_FACE",FACE,{"disambiguationData":[OSD([subQ0])]});var subQ2=makeQuery(id+"F1.opExtrude","CAP_EDGE",EDGE,{"disambiguationData":[OSD([subQ0])],"isStart":true});Q28=makeQuery(id+"F4.boolean.opBoolean","SPLIT",EDGE,{"disambiguationData":[TD([makeQuery(id+"F4.opExtrude","SWEPT_FACE",FACE,{"disambiguationData":[OSD([sQuery(id+"F2.wireOp",EDGE,"E2.9.0.1")])]})])],"derivedFrom":makeQuery(id+"F3.opChamfer","BLEND_EDGE",EDGE,{"blendedFrom":[subQ2,subQ1],"blendedInto":[subQ1]})});}
            var Q29;
            {var subQ0=sQuery(id+"F0.wireOp",EDGE,"E0.top");var subQ1=makeQuery(id+"F1.opExtrude","SWEPT_FACE",FACE,{"disambiguationData":[OSD([subQ0])]});var subQ2=makeQuery(id+"F1.opExtrude","CAP_EDGE",EDGE,{"disambiguationData":[OSD([subQ0])],"isStart":true});Q29=makeQuery(id+"F4.boolean.opBoolean","SPLIT",EDGE,{"disambiguationData":[TD([makeQuery(id+"F4.opExtrude","SWEPT_FACE",FACE,{"disambiguationData":[OSD([sQuery(id+"F2.wireOp",EDGE,"E2.8.0.1")])]})])],"derivedFrom":makeQuery(id+"F3.opChamfer","BLEND_EDGE",EDGE,{"blendedFrom":[subQ2,subQ1],"blendedInto":[subQ1]})});}
            var Q30;
            {var subQ0=sQuery(id+"F0.wireOp",EDGE,"E0.top");var subQ1=makeQuery(id+"F1.opExtrude","SWEPT_FACE",FACE,{"disambiguationData":[OSD([subQ0])]});var subQ2=makeQuery(id+"F1.opExtrude","CAP_EDGE",EDGE,{"disambiguationData":[OSD([subQ0])],"isStart":true});Q30=makeQuery(id+"F4.boolean.opBoolean","SPLIT",EDGE,{"disambiguationData":[TD([makeQuery(id+"F4.opExtrude","SWEPT_FACE",FACE,{"disambiguationData":[OSD([sQuery(id+"F2.wireOp",EDGE,"E2.7.0.1")])]})])],"derivedFrom":makeQuery(id+"F3.opChamfer","BLEND_EDGE",EDGE,{"blendedFrom":[subQ2,subQ1],"blendedInto":[subQ1]})});}
            var Q31;
            {var subQ0=sQuery(id+"F0.wireOp",EDGE,"E0.top");var subQ1=makeQuery(id+"F1.opExtrude","SWEPT_FACE",FACE,{"disambiguationData":[OSD([subQ0])]});var subQ2=makeQuery(id+"F1.opExtrude","CAP_EDGE",EDGE,{"disambiguationData":[OSD([subQ0])],"isStart":true});Q31=makeQuery(id+"F4.boolean.opBoolean","SPLIT",EDGE,{"disambiguationData":[TD([makeQuery(id+"F4.opExtrude","SWEPT_FACE",FACE,{"disambiguationData":[OSD([sQuery(id+"F2.wireOp",EDGE,"E2.6.0.1")])]})])],"derivedFrom":makeQuery(id+"F3.opChamfer","BLEND_EDGE",EDGE,{"blendedFrom":[subQ2,subQ1],"blendedInto":[subQ1]})});}
            var Q32;
            {var subQ0=sQuery(id+"F0.wireOp",EDGE,"E0.top");var subQ1=makeQuery(id+"F1.opExtrude","SWEPT_FACE",FACE,{"disambiguationData":[OSD([subQ0])]});var subQ2=makeQuery(id+"F1.opExtrude","CAP_EDGE",EDGE,{"disambiguationData":[OSD([subQ0])],"isStart":true});Q32=makeQuery(id+"F4.boolean.opBoolean","SPLIT",EDGE,{"disambiguationData":[TD([makeQuery(id+"F4.opExtrude","SWEPT_FACE",FACE,{"disambiguationData":[OSD([sQuery(id+"F2.wireOp",EDGE,"E2.5.0.1")])]})])],"derivedFrom":makeQuery(id+"F3.opChamfer","BLEND_EDGE",EDGE,{"blendedFrom":[subQ2,subQ1],"blendedInto":[subQ1]})});}
            var Q33;
            {var subQ0=sQuery(id+"F0.wireOp",EDGE,"E0.top");var subQ1=makeQuery(id+"F1.opExtrude","SWEPT_FACE",FACE,{"disambiguationData":[OSD([subQ0])]});var subQ2=makeQuery(id+"F1.opExtrude","CAP_EDGE",EDGE,{"disambiguationData":[OSD([subQ0])],"isStart":true});Q33=makeQuery(id+"F4.boolean.opBoolean","SPLIT",EDGE,{"disambiguationData":[TD([makeQuery(id+"F4.opExtrude","SWEPT_FACE",FACE,{"disambiguationData":[OSD([sQuery(id+"F2.wireOp",EDGE,"E2.4.0.1")])]})])],"derivedFrom":makeQuery(id+"F3.opChamfer","BLEND_EDGE",EDGE,{"blendedFrom":[subQ2,subQ1],"blendedInto":[subQ1]})});}
            var Q34;
            {var subQ0=sQuery(id+"F0.wireOp",EDGE,"E0.top");var subQ1=makeQuery(id+"F1.opExtrude","SWEPT_FACE",FACE,{"disambiguationData":[OSD([subQ0])]});var subQ2=makeQuery(id+"F1.opExtrude","CAP_EDGE",EDGE,{"disambiguationData":[OSD([subQ0])],"isStart":true});Q34=makeQuery(id+"F4.boolean.opBoolean","SPLIT",EDGE,{"disambiguationData":[TD([makeQuery(id+"F4.opExtrude","SWEPT_FACE",FACE,{"disambiguationData":[OSD([sQuery(id+"F2.wireOp",EDGE,"E2.3.0.1")])]})])],"derivedFrom":makeQuery(id+"F3.opChamfer","BLEND_EDGE",EDGE,{"blendedFrom":[subQ2,subQ1],"blendedInto":[subQ1]})});}
            var Q35;
            {var subQ0=sQuery(id+"F0.wireOp",EDGE,"E0.top");var subQ1=makeQuery(id+"F1.opExtrude","SWEPT_FACE",FACE,{"disambiguationData":[OSD([subQ0])]});var subQ2=makeQuery(id+"F1.opExtrude","CAP_EDGE",EDGE,{"disambiguationData":[OSD([subQ0])],"isStart":true});Q35=makeQuery(id+"F4.boolean.opBoolean","SPLIT",EDGE,{"disambiguationData":[TD([makeQuery(id+"F4.opExtrude","SWEPT_FACE",FACE,{"disambiguationData":[OSD([sQuery(id+"F2.wireOp",EDGE,"E2.2.0.1")])]})])],"derivedFrom":makeQuery(id+"F3.opChamfer","BLEND_EDGE",EDGE,{"blendedFrom":[subQ2,subQ1],"blendedInto":[subQ1]})});}
            var Q36;
            {var subQ0=sQuery(id+"F0.wireOp",EDGE,"E0.top");var subQ1=makeQuery(id+"F1.opExtrude","SWEPT_FACE",FACE,{"disambiguationData":[OSD([subQ0])]});var subQ2=makeQuery(id+"F1.opExtrude","CAP_EDGE",EDGE,{"disambiguationData":[OSD([subQ0])],"isStart":true});Q36=makeQuery(id+"F4.boolean.opBoolean","SPLIT",EDGE,{"disambiguationData":[TD([makeQuery(id+"F4.opExtrude","SWEPT_FACE",FACE,{"disambiguationData":[OSD([sQuery(id+"F2.wireOp",EDGE,"E2.1.0.1")])]})])],"derivedFrom":makeQuery(id+"F3.opChamfer","BLEND_EDGE",EDGE,{"blendedFrom":[subQ2,subQ1],"blendedInto":[subQ1]})});}
            var Q37;
            {var subQ0=sQuery(id+"F0.wireOp",EDGE,"E0.top");var subQ1=makeQuery(id+"F1.opExtrude","SWEPT_FACE",FACE,{"disambiguationData":[OSD([subQ0])]});var subQ2=makeQuery(id+"F1.opExtrude","CAP_EDGE",EDGE,{"disambiguationData":[OSD([subQ0])],"isStart":true});Q37=makeQuery(id+"F4.boolean.opBoolean","SPLIT",EDGE,{"disambiguationData":[TD([makeQuery(id+"F4.opExtrude","SWEPT_FACE",FACE,{"disambiguationData":[OSD([sQuery(id+"F2.wireOp",EDGE,"E1.left")])]})])],"derivedFrom":makeQuery(id+"F3.opChamfer","BLEND_EDGE",EDGE,{"blendedFrom":[subQ2,subQ1],"blendedInto":[subQ1]})});}
            var Q38;
            {var subQ0=sQuery(id+"F0.wireOp",EDGE,"E0.top");var subQ1=makeQuery(id+"F1.opExtrude","SWEPT_FACE",FACE,{"disambiguationData":[OSD([subQ0])]});var subQ2=makeQuery(id+"F1.opExtrude","CAP_EDGE",EDGE,{"disambiguationData":[OSD([subQ0])],"isStart":false});Q38=makeQuery(id+"F4.boolean.opBoolean","SPLIT",EDGE,{"disambiguationData":[TD([makeQuery(id+"F1.opExtrude","SWEPT_FACE",FACE,{"disambiguationData":[OSD([sQuery(id+"F0.wireOp",EDGE,"E0.right")])]})])],"derivedFrom":makeQuery(id+"F3.opChamfer","BLEND_EDGE",EDGE,{"blendedFrom":[subQ2,subQ1],"blendedInto":[subQ1]})});}
            var Q39;
            {var subQ0=sQuery(id+"F0.wireOp",EDGE,"E0.top");var subQ1=makeQuery(id+"F1.opExtrude","SWEPT_FACE",FACE,{"disambiguationData":[OSD([subQ0])]});var subQ2=makeQuery(id+"F1.opExtrude","CAP_EDGE",EDGE,{"disambiguationData":[OSD([subQ0])],"isStart":true});Q39=makeQuery(id+"F4.boolean.opBoolean","SPLIT",EDGE,{"disambiguationData":[TD([makeQuery(id+"F1.opExtrude","SWEPT_FACE",FACE,{"disambiguationData":[OSD([sQuery(id+"F0.wireOp",EDGE,"E0.right")])]})])],"derivedFrom":makeQuery(id+"F3.opChamfer","BLEND_EDGE",EDGE,{"blendedFrom":[subQ2,subQ1],"blendedInto":[subQ1]})});}
            fillet(context, id + "F7", {"entities" : qUnion([Q0, Q1, Q2, Q3, Q4, Q5, Q6, Q7, Q8, Q9, Q10, Q11, Q12, Q13, Q14, Q15, Q16, Q17, Q18, Q19, Q20, Q21, Q22, Q23, Q24, Q25, Q26, Q27, Q28, Q29, Q30, Q31, Q32, Q33, Q34, Q35, Q36, Q37, Q38, Q39]), "radius" : 0.5 * mm, "tangentPropagation" : true, "allowEdgeOverflow" : false});
        }
        {
            var Q0;
            Q0=makeQuery(id+"F1.opExtrude","CAP_FACE",FACE,{"disambiguationData":[OSD([sQuery(id+"F0.wireOp",EDGE,"E0.bottom"),sQuery(id+"F0.wireOp",EDGE,"E0.top"),sQuery(id+"F0.wireOp",EDGE,"E0.left"),sQuery(id+"F0.wireOp",EDGE,"E0.right")])],"isStart":false});
            var sketch = newSketch(context, id + "F8", { "sketchPlane" : qUnion([Q0])});
            skText(sketch, "E3", { "text": "依彤", "fontName": "NotoSansCJKtc-Regular.otf"});
            const initialGuessF8  = {"E3": [-0.05193, 0.02878, 1, 0, 0.00643]};
            skSetInitialGuess(sketch, initialGuessF8);
            skSolve(sketch);
        }
        {
            var Q0;
            Q0=makeQuery(id+"F8.imprint","IMPRINT",FACE,{"disambiguationData":[TD([[makeQuery(id+"F8.imprint","IMPRINT",EDGE,{"derivedFrom":sQuery(id+"F8.wireOp",EDGE,"E3.sketch_text.stroke-44")}),1.0]])]});
            extrude(context, id + "F9", {"entities" : qUnion([Q0]), "operationType" : NewBodyOperationType.REMOVE, "oppositeDirection" : true, "depth" : 0.5 * mm});
        }
        {
            var Q0;
            Q0 = qSketchRegion(id + "F8", true);
            extrude(context, id + "F10", {"entities" : qUnion([Q0]), "operationType" : NewBodyOperationType.REMOVE, "oppositeDirection" : true, "depth" : 0.5 * mm});
        }
        {
            var Q0;
            Q0=makeQuery(id+"F8.imprint","IMPRINT",FACE,{"disambiguationData":[TD([[makeQuery(id+"F8.imprint","IMPRINT",EDGE,{"derivedFrom":sQuery(id+"F8.wireOp",EDGE,"E3.sketch_text.stroke-0")}),-1.0]])]});
            var sketch = newSketch(context, id + "F11", { "sketchPlane" : qUnion([Q0])});
            skText(sketch, "E4", { "text": "資淳", "fontName": "NotoSansCJKtc-Regular.otf"});
            const initialGuessF11  = {"E4": [-0.0519, 0.03985, 1, 0, 0.00644]};
            skSetInitialGuess(sketch, initialGuessF11);
            skSolve(sketch);
        }
        {
            var Q0;
            Q0 = qSketchRegion(id + "F11", true);
            extrude(context, id + "F12", {"entities" : qUnion([Q0]), "operationType" : NewBodyOperationType.REMOVE, "oppositeDirection" : true, "depth" : 0.5 * mm});
        }
    });
